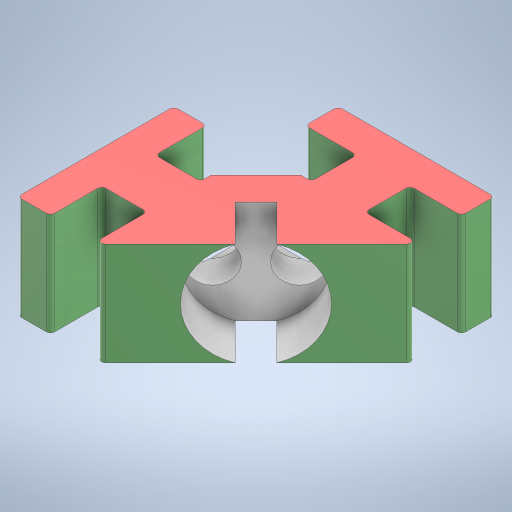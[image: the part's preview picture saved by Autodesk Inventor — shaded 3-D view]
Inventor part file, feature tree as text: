
AUTODESK INVENTOR PART (.ipt)
format: ipt  version: 2023 (Build 270158000, 158)  size: 346,112 bytes
history: native  units: in
note: dims shown in document units (in); Inventor stores cm internally (conversion verified against a paired STEP export)
features: other x4, extrude x3, sketch x3
ambient origin geometry x8: Origin, YZ Plane, XZ Plane, XY Plane, X Axis, Y Axis, Z Axis, Center Point
bodies: Body1 (feature_tree)
feature tree (10):
  other  "TmpPart3.ipt"
  extrude  "Extrusion1"  Depth=0.3937in
  extrude  "Extrusion2"  Depth=0.0591in
  extrude  "Extrusion3"  Depth=0.126in TaperAngle=0.0deg
  other  "PLA2::TmpPart3.ipt"
  other  "TaggingFeature1"
  sketch  "Sketch1"  dims[d0=0.3937in d1=0.2047in]
  sketch  "Sketch2"  dims[d2=0.0984in d3=0.0in d4=0.0591in]
  sketch  "Sketch3"  dims[d5=0.0787in d6=0.126in d7=0.0in d8=0.0787in d9=0.0787in d10=0.1378in d11=0.0in]
  other  "PLA2"
